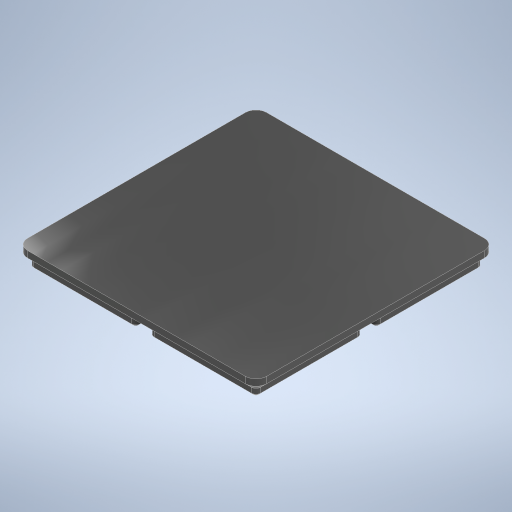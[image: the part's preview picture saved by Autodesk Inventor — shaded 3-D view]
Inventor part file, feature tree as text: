
AUTODESK INVENTOR PART (.ipt)
format: ipt  version: 2023 (Build 270158030, 158C)  size: 434,688 bytes
history: native  units: mm
features: extrude x7, sketch x7, projected_geometry x3, pattern_linear x1
ambient origin geometry x8: Origin, YZ Plane, XZ Plane, XY Plane, X Axis, Y Axis, Z Axis, Center Point
bodies: Solid2 (feature_tree)
feature tree (18):
  extrude  "base-generic"  Depth=41.5mm
  extrude  "Extrusion8"  Depth=2.25mm TaperAngle=0.0deg
  extrude  "Extrusion9"  Depth=2.15mm
  extrude  "Extrusion10"  Depth=0.8mm
  extrude  "Extrusion11"  Depth=7.75mm
  extrude  "Extrusion12"  Depth=7.75mm
  pattern_linear  "Rectangular Pattern1"  Spacing1=2.4mm  [1 undecoded]
  extrude  "Extrusion13"  Depth=2.25mm
  sketch  "Sketch9"  dims[d50=41.5mm d51=41.5mm]
  sketch  "Sketch10"  dims[d52=3.75mm d53=2.25mm d54=0.0mm]
  projected_geometry  "Projected Loop2"
  sketch  "Sketch11"  dims[d55=3.75mm d56=2.15mm d57=-7.853982mm]
  projected_geometry  "Projected Loop3"
  sketch  "Sketch12"  dims[d58=1.8mm d59=0.0mm d60=0.8mm d61=-7.853982mm]
  projected_geometry  "Projected Loop4"
  sketch  "Sketch13"  dims[d62=6.5mm d63=7.75mm]
  sketch  "Sketch14"  dims[d64=7.75mm d65=7.75mm]
  sketch  "Sketch15"  dims[d66=7.75mm d67=2.4mm d68=0.0mm d69=3.0mm d70=6.0mm d71=0.0mm d72=20.0mm d74=42.0mm d75=20.0mm d77=42.0mm d78=3.75mm d79=2.25mm d80=0.0mm d17=0.5mm d18=0.872665mm d19=0.5mm d20=0.872665mm d24=0.0mm d25=0.0mm d26=0.0mm d27=0.0mm]
note: 1 required parameter value undecoded (feature->parameter linkage not recoverable at this tier; creation-order binding heuristic only, values carry confidence <= 0.55)
